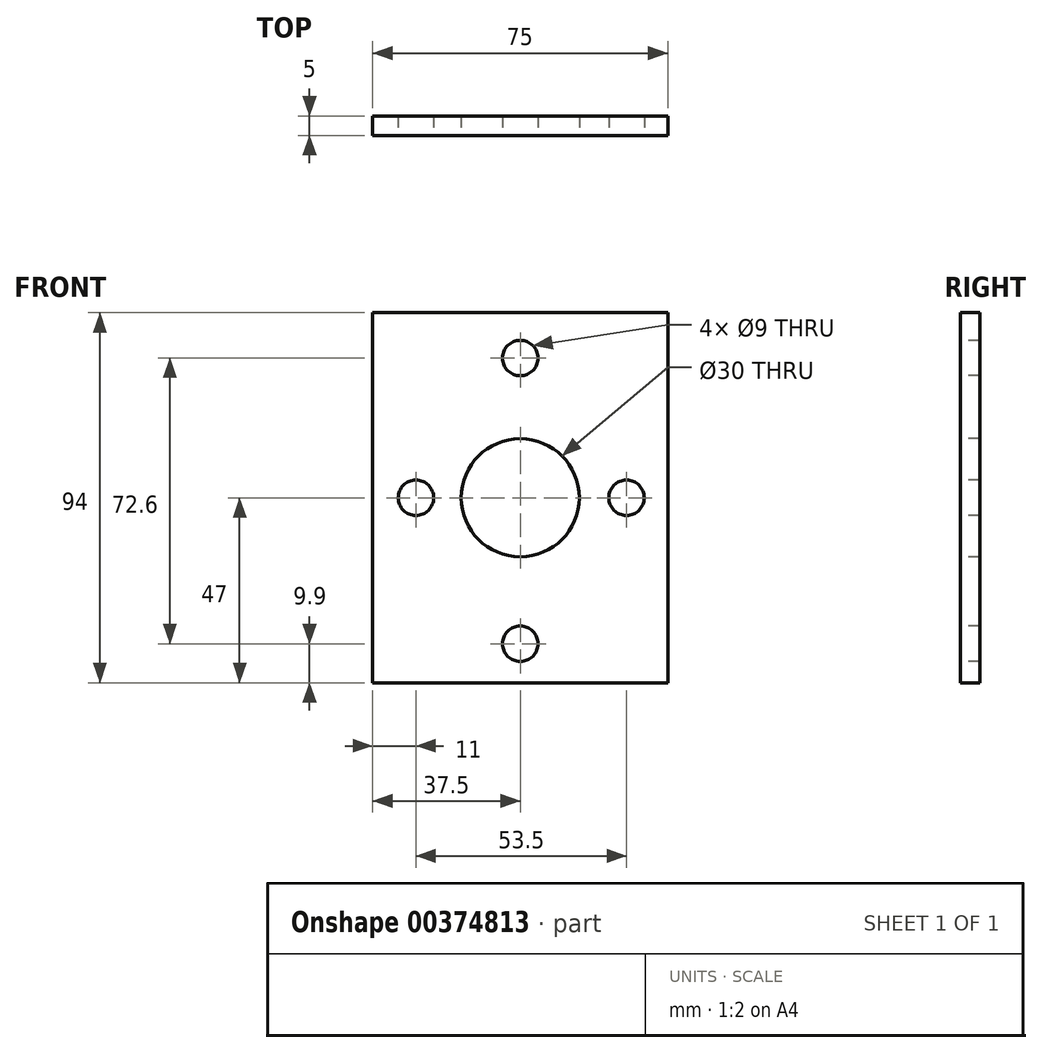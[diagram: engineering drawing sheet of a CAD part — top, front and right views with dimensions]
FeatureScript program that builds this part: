
annotation { "Feature Type Name" : "Feature", "Feature Type Description" : "" }
export const myFeature = defineFeature(function(context is Context, id is Id, definition is map)
    precondition{}
    {
        {
            var Q0;
            Q0=qCreatedBy(makeId("Front.planeOp"),FACE);
            var sketch = newSketch(context, id + "F0", { "sketchPlane" : qUnion([Q0])});
            skLineSegment(sketch, "E0.bottom", {"start": v(37.5, -47) * mm, "end": v(-37.5, -47) * mm});
            skLineSegment(sketch, "E0.top", {"start": v(37.5, 47) * mm, "end": v(-37.5, 47) * mm});
            skLineSegment(sketch, "E0.left", {"start": v(37.5, -47) * mm, "end": v(37.5, 47) * mm});
            skLineSegment(sketch, "E0.right", {"start": v(-37.5, -47) * mm, "end": v(-37.5, 47) * mm});
            skPoint(sketch, "E0.middle", {"position": v(0, 0) * mm});
            skSolve(sketch);
        }
        {
            var Q0;
            Q0 = qSketchRegion(id + "F0", true);
            extrude(context, id + "F1", {"entities" : qUnion([Q0]), "oppositeDirection" : true, "depth" : 5 * mm, "offsetDistance" : 25 * mm});
        }
        {
            var Q0;
            Q0=makeQuery(id+"F1.opExtrude","CAP_FACE",FACE,{"disambiguationData":[OSD([sQuery(id+"F0.wireOp",EDGE,"E0.bottom"),sQuery(id+"F0.wireOp",EDGE,"E0.top"),sQuery(id+"F0.wireOp",EDGE,"E0.left"),sQuery(id+"F0.wireOp",EDGE,"E0.right")])],"isStart":true});
            var sketch = newSketch(context, id + "F2", { "sketchPlane" : qUnion([Q0])});
            skCircle(sketch, "E1", {"center": v(0, 35.5) * mm, "radius": 4.5 * mm});
            skCircle(sketch, "E2", {"center": v(0, -37.1) * mm, "radius": 4.5 * mm});
            skCircle(sketch, "E3", {"center": v(27, 0) * mm, "radius": 4.5 * mm});
            skCircle(sketch, "E4", {"center": v(-26.5, 0) * mm, "radius": 4.5 * mm});
            skCircle(sketch, "E5", {"center": v(0, 0) * mm, "radius": 15 * mm});
            skSolve(sketch);
        }
        {
            var Q0;
            Q0=makeQuery(id+"F2.imprint","IMPRINT",FACE,{"disambiguationData":[TD([[makeQuery(id+"F2.imprint","IMPRINT",EDGE,{"derivedFrom":sQuery(id+"F2.wireOp",EDGE,"E5")}),1.0]])]});
            var Q1;
            Q1=makeQuery(id+"F2.imprint","IMPRINT",FACE,{"disambiguationData":[TD([[makeQuery(id+"F2.imprint","IMPRINT",EDGE,{"derivedFrom":sQuery(id+"F2.wireOp",EDGE,"E1")}),1.0]])]});
            var Q2;
            Q2=makeQuery(id+"F2.imprint","IMPRINT",FACE,{"disambiguationData":[TD([[makeQuery(id+"F2.imprint","IMPRINT",EDGE,{"derivedFrom":sQuery(id+"F2.wireOp",EDGE,"E4")}),1.0]])]});
            var Q3;
            Q3=makeQuery(id+"F2.imprint","IMPRINT",FACE,{"disambiguationData":[TD([[makeQuery(id+"F2.imprint","IMPRINT",EDGE,{"derivedFrom":sQuery(id+"F2.wireOp",EDGE,"E3")}),1.0]])]});
            var Q4;
            Q4=makeQuery(id+"F2.imprint","IMPRINT",FACE,{"disambiguationData":[TD([[makeQuery(id+"F2.imprint","IMPRINT",EDGE,{"derivedFrom":sQuery(id+"F2.wireOp",EDGE,"E2")}),1.0]])]});
            var Q5;
            Q5=makeQuery(id+"F1.opExtrude","CAP_FACE",FACE,{"disambiguationData":[OSD([sQuery(id+"F0.wireOp",EDGE,"E0.bottom"),sQuery(id+"F0.wireOp",EDGE,"E0.top"),sQuery(id+"F0.wireOp",EDGE,"E0.left"),sQuery(id+"F0.wireOp",EDGE,"E0.right")])],"isStart":false});
            extrude(context, id + "F3", {"entities" : qUnion([Q0, Q1, Q2, Q3, Q4]), "operationType" : NewBodyOperationType.REMOVE, "endBound" : BoundingType.UP_TO_SURFACE, "oppositeDirection" : true, "depth" : 25 * mm, "endBoundEntityFace" : qUnion([Q5]), "offsetDistance" : 25 * mm});
        }
    });
